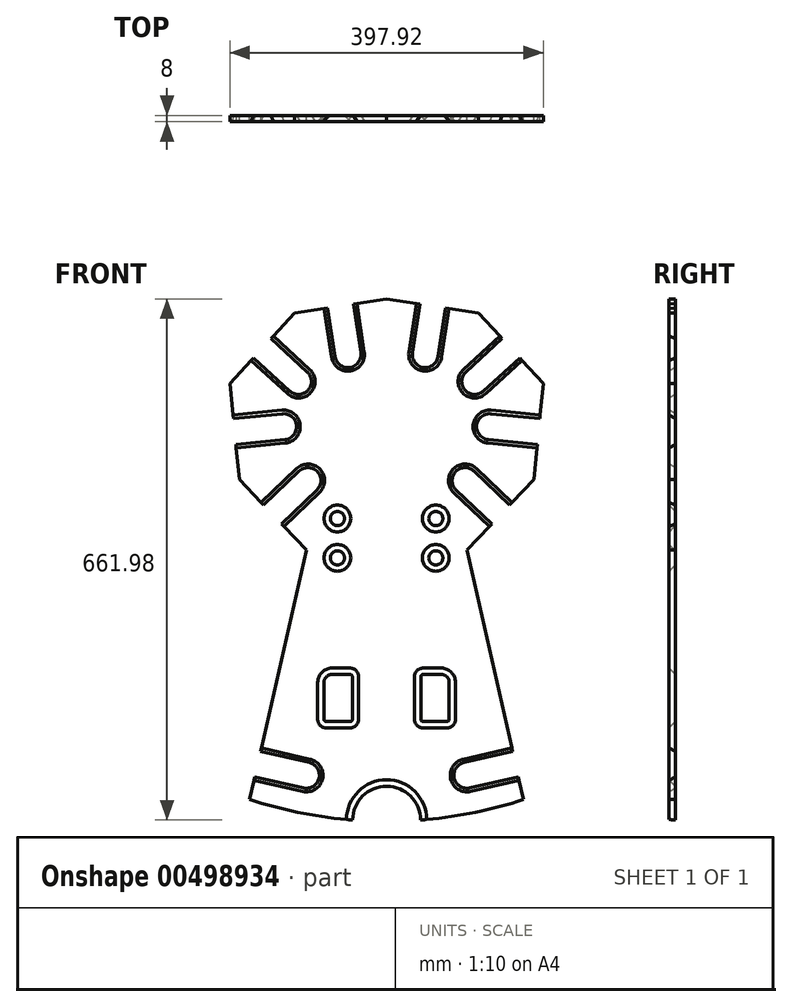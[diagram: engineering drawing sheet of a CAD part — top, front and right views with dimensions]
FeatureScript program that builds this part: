
annotation { "Feature Type Name" : "Feature", "Feature Type Description" : "" }
export const myFeature = defineFeature(function(context is Context, id is Id, definition is map)
    precondition{}
    {
        {
            var Q0;
            Q0=qCreatedBy(makeId("Front.planeOp"),FACE);
            var sketch = newSketch(context, id + "F0", { "sketchPlane" : qUnion([Q0])});
            skArc(sketch, "E0", {"start": v(43, -331) * mm, "mid": v(109.28, -321.9) * mm, "end": v(174, -305) * mm});
            skLineSegment(sketch, "E1", {"start": v(167.46, -276.23) * mm, "end": v(105.54, -290.3) * mm});
            skLineSegment(sketch, "E2", {"start": v(98.23, -258.12) * mm, "end": v(160.15, -244.05) * mm});
            skArc(sketch, "E3", {"start": v(98.23, -258.12) * mm, "mid": v(85.8, -277.87) * mm, "end": v(105.54, -290.3) * mm});
            skLineSegment(sketch, "E4", {"start": v(133.66, 45.23) * mm, "end": v(88.34, 88.26) * mm});
            skLineSegment(sketch, "E5", {"start": v(111.06, 112.2) * mm, "end": v(156.39, 69.16) * mm});
            skArc(sketch, "E6", {"start": v(111.06, 112.2) * mm, "mid": v(87.73, 111.59) * mm, "end": v(88.34, 88.26) * mm});
            skLineSegment(sketch, "E7", {"start": v(191.4, 146.18) * mm, "end": v(129.2, 152.25) * mm});
            skLineSegment(sketch, "E8", {"start": v(132.4, 185.1) * mm, "end": v(194.6, 179.02) * mm});
            skArc(sketch, "E9", {"start": v(132.4, 185.1) * mm, "mid": v(114.38, 170.27) * mm, "end": v(129.2, 152.25) * mm});
            skLineSegment(sketch, "E10", {"start": v(169.16, 256.17) * mm, "end": v(123.1, 213.93) * mm});
            skLineSegment(sketch, "E11", {"start": v(100.8, 238.26) * mm, "end": v(146.86, 280.5) * mm});
            skArc(sketch, "E12", {"start": v(100.8, 238.26) * mm, "mid": v(99.78, 214.95) * mm, "end": v(123.1, 213.93) * mm});
            skLineSegment(sketch, "E13", {"start": v(74.9, 319.52) * mm, "end": v(65.44, 257.74) * mm});
            skLineSegment(sketch, "E14", {"start": v(32.82, 262.74) * mm, "end": v(42.29, 324.52) * mm});
            skArc(sketch, "E15", {"start": v(32.82, 262.74) * mm, "mid": v(46.64, 243.93) * mm, "end": v(65.44, 257.74) * mm});
            skArc(sketch, "E16", {"start": v(-174, -305) * mm, "mid": v(-109.28, -321.9) * mm, "end": v(-43, -331) * mm});
            skLineSegment(sketch, "E17", {"start": v(-167.46, -276.23) * mm, "end": v(-105.54, -290.3) * mm});
            skLineSegment(sketch, "E18", {"start": v(-98.23, -258.12) * mm, "end": v(-160.15, -244.05) * mm});
            skArc(sketch, "E19", {"start": v(-105.54, -290.3) * mm, "mid": v(-85.8, -277.87) * mm, "end": v(-98.23, -258.12) * mm});
            skLineSegment(sketch, "E20", {"start": v(-133.66, 45.23) * mm, "end": v(-88.34, 88.26) * mm});
            skLineSegment(sketch, "E21", {"start": v(-111.06, 112.2) * mm, "end": v(-156.39, 69.16) * mm});
            skArc(sketch, "E22", {"start": v(-88.34, 88.26) * mm, "mid": v(-87.73, 111.59) * mm, "end": v(-111.06, 112.2) * mm});
            skLineSegment(sketch, "E23", {"start": v(-191.4, 146.18) * mm, "end": v(-129.2, 152.25) * mm});
            skLineSegment(sketch, "E24", {"start": v(-132.4, 185.1) * mm, "end": v(-194.6, 179.02) * mm});
            skArc(sketch, "E25", {"start": v(-129.2, 152.25) * mm, "mid": v(-114.38, 170.27) * mm, "end": v(-132.4, 185.1) * mm});
            skLineSegment(sketch, "E26", {"start": v(-169.16, 256.17) * mm, "end": v(-123.1, 213.93) * mm});
            skLineSegment(sketch, "E27", {"start": v(-100.8, 238.26) * mm, "end": v(-146.86, 280.5) * mm});
            skArc(sketch, "E28", {"start": v(-123.1, 213.93) * mm, "mid": v(-99.78, 214.95) * mm, "end": v(-100.8, 238.26) * mm});
            skLineSegment(sketch, "E29", {"start": v(-74.9, 319.52) * mm, "end": v(-65.44, 257.74) * mm});
            skLineSegment(sketch, "E30", {"start": v(-32.82, 262.74) * mm, "end": v(-42.29, 324.52) * mm});
            skArc(sketch, "E31", {"start": v(-65.44, 257.74) * mm, "mid": v(-46.64, 243.93) * mm, "end": v(-32.82, 262.74) * mm});
            skArc(sketch, "E32", {"start": v(43, -331) * mm, "mid": v(0, -288) * mm, "end": v(-43, -331) * mm});
            skCircle(sketch, "E33", {"center": v(-62.5, 52) * mm, "radius": 9 * mm});
            skCircle(sketch, "E34", {"center": v(62.5, 52) * mm, "radius": 9 * mm});
            skCircle(sketch, "E35", {"center": v(-62.5, 2) * mm, "radius": 9 * mm});
            skCircle(sketch, "E36", {"center": v(62.5, 2) * mm, "radius": 9 * mm});
            skLineSegment(sketch, "E37", {"start": v(-43.5, -146) * mm, "end": v(-43.5, -206) * mm});
            skLineSegment(sketch, "E38", {"start": v(43.5, -146) * mm, "end": v(43.5, -206) * mm});
            skLineSegment(sketch, "E39", {"start": v(-69.5, -146) * mm, "end": v(-43.5, -146) * mm});
            skLineSegment(sketch, "E40", {"start": v(-79.5, -206) * mm, "end": v(-43.5, -206) * mm});
            skLineSegment(sketch, "E41", {"start": v(-79.5, -156) * mm, "end": v(-79.5, -206) * mm});
            skLineSegment(sketch, "E42", {"start": v(79.5, -156) * mm, "end": v(79.5, -206) * mm});
            skLineSegment(sketch, "E43", {"start": v(43.5, -146) * mm, "end": v(69.5, -146) * mm});
            skLineSegment(sketch, "E44", {"start": v(43.5, -206) * mm, "end": v(79.5, -206) * mm});
            skArc(sketch, "E45", {"start": v(79.5, -156) * mm, "mid": v(76.57, -148.92) * mm, "end": v(69.5, -146) * mm});
            skArc(sketch, "E46", {"start": v(-69.5, -146) * mm, "mid": v(-76.57, -148.92) * mm, "end": v(-79.5, -156) * mm});
            skLineSegment(sketch, "E47", {"start": v(-133.66, 45.23) * mm, "end": v(-102, 11.87) * mm});
            skLineSegment(sketch, "E48", {"start": v(-187.04, 101.45) * mm, "end": v(-156.39, 69.16) * mm});
            skLineSegment(sketch, "E49", {"start": v(-191.4, 146.18) * mm, "end": v(-187.04, 101.45) * mm});
            skLineSegment(sketch, "E50", {"start": v(-198.96, 223.66) * mm, "end": v(-194.6, 179.02) * mm});
            skLineSegment(sketch, "E51", {"start": v(-169.16, 256.17) * mm, "end": v(-198.96, 223.66) * mm});
            skLineSegment(sketch, "E52", {"start": v(-117, 313.07) * mm, "end": v(-146.86, 280.5) * mm});
            skLineSegment(sketch, "E53", {"start": v(-74.9, 319.52) * mm, "end": v(-117, 313.07) * mm});
            skLineSegment(sketch, "E54", {"start": v(0, 331) * mm, "end": v(-42.29, 324.52) * mm});
            skLineSegment(sketch, "E55", {"start": v(0, 331) * mm, "end": v(42.29, 324.52) * mm});
            skLineSegment(sketch, "E56", {"start": v(74.9, 319.52) * mm, "end": v(117, 313.07) * mm});
            skLineSegment(sketch, "E57", {"start": v(117, 313.07) * mm, "end": v(146.86, 280.5) * mm});
            skLineSegment(sketch, "E58", {"start": v(169.16, 256.17) * mm, "end": v(198.96, 223.66) * mm});
            skLineSegment(sketch, "E59", {"start": v(198.96, 223.66) * mm, "end": v(194.6, 179.02) * mm});
            skLineSegment(sketch, "E60", {"start": v(191.4, 146.18) * mm, "end": v(187.04, 101.45) * mm});
            skLineSegment(sketch, "E61", {"start": v(187.04, 101.45) * mm, "end": v(156.39, 69.16) * mm});
            skLineSegment(sketch, "E62", {"start": v(133.66, 45.23) * mm, "end": v(102, 11.87) * mm});
            skLineSegment(sketch, "E63", {"start": v(-102, 11.87) * mm, "end": v(-160.15, -244.05) * mm});
            skLineSegment(sketch, "E64", {"start": v(102, 11.87) * mm, "end": v(160.15, -244.05) * mm});
            skLineSegment(sketch, "E65", {"start": v(-167.46, -276.23) * mm, "end": v(-174, -305) * mm});
            skLineSegment(sketch, "E66", {"start": v(167.46, -276.23) * mm, "end": v(174, -305) * mm});
            skSolve(sketch);
        }
        {
            var Q0;
            Q0 = qSketchRegion(id + "F0", true);
            extrude(context, id + "F1", {"entities" : qUnion([Q0]), "depth" : 8 * mm});
        }
        {
            var Q0;
            Q0=makeQuery(id+"F1.opExtrude","SWEPT_EDGE",EDGE,{"disambiguationData":[OSD([sQuery(id+"F0.wireOp",EDGE,"E37"),sQuery(id+"F0.wireOp",EDGE,"E40")])]});
            var Q1;
            Q1=makeQuery(id+"F1.opExtrude","SWEPT_EDGE",EDGE,{"disambiguationData":[OSD([sQuery(id+"F0.wireOp",EDGE,"E42"),sQuery(id+"F0.wireOp",EDGE,"E44")])]});
            var Q2;
            Q2=makeQuery(id+"F1.opExtrude","SWEPT_EDGE",EDGE,{"disambiguationData":[OSD([sQuery(id+"F0.wireOp",EDGE,"E38"),sQuery(id+"F0.wireOp",EDGE,"E44")])]});
            var Q3;
            Q3=makeQuery(id+"F1.opExtrude","SWEPT_EDGE",EDGE,{"disambiguationData":[OSD([sQuery(id+"F0.wireOp",EDGE,"E40"),sQuery(id+"F0.wireOp",EDGE,"E41")])]});
            var Q4;
            Q4=makeQuery(id+"F1.opExtrude","SWEPT_EDGE",EDGE,{"disambiguationData":[OSD([sQuery(id+"F0.wireOp",EDGE,"E37"),sQuery(id+"F0.wireOp",EDGE,"E39")])]});
            var Q5;
            Q5=makeQuery(id+"F1.opExtrude","SWEPT_EDGE",EDGE,{"disambiguationData":[OSD([sQuery(id+"F0.wireOp",EDGE,"E38"),sQuery(id+"F0.wireOp",EDGE,"E43")])]});
            fillet(context, id + "F2", {"entities" : qUnion([Q0, Q1, Q2, Q3, Q4, Q5]), "radius" : 3 * mm, "tangentPropagation" : true, "allowEdgeOverflow" : false});
        }
        {
            var Q0;
            Q0=makeQuery(id+"F1.opExtrude","CAP_EDGE",EDGE,{"disambiguationData":[OSD([sQuery(id+"F0.wireOp",EDGE,"E33")])],"isStart":false});
            var Q1;
            Q1=makeQuery(id+"F1.opExtrude","CAP_EDGE",EDGE,{"disambiguationData":[OSD([sQuery(id+"F0.wireOp",EDGE,"E34")])],"isStart":false});
            var Q2;
            Q2=makeQuery(id+"F1.opExtrude","CAP_EDGE",EDGE,{"disambiguationData":[OSD([sQuery(id+"F0.wireOp",EDGE,"E35")])],"isStart":false});
            var Q3;
            Q3=makeQuery(id+"F1.opExtrude","CAP_EDGE",EDGE,{"disambiguationData":[OSD([sQuery(id+"F0.wireOp",EDGE,"E36")])],"isStart":false});
            var Q4;
            Q4=makeQuery(id+"F1.opExtrude","CAP_EDGE",EDGE,{"disambiguationData":[OSD([sQuery(id+"F0.wireOp",EDGE,"E39")])],"isStart":false});
            var Q5;
            Q5=makeQuery(id+"F1.opExtrude","CAP_EDGE",EDGE,{"disambiguationData":[OSD([sQuery(id+"F0.wireOp",EDGE,"E43")])],"isStart":false});
            var Q6;
            Q6=makeQuery(id+"F1.opExtrude","CAP_EDGE",EDGE,{"disambiguationData":[OSD([sQuery(id+"F0.wireOp",EDGE,"E32")])],"isStart":false});
            chamfer(context, id + "F3", {"entities" : qUnion([Q0, Q1, Q2, Q3, Q4, Q5, Q6]), "width" : 8 * mm, "tangentPropagation" : true});
        }
        {
            var Q0;
            Q0=makeQuery(id+"F1.opExtrude","CAP_EDGE",EDGE,{"disambiguationData":[OSD([sQuery(id+"F0.wireOp",EDGE,"E21")])],"isStart":false});
            var Q1;
            Q1=makeQuery(id+"F1.opExtrude","CAP_EDGE",EDGE,{"disambiguationData":[OSD([sQuery(id+"F0.wireOp",EDGE,"E24")])],"isStart":false});
            var Q2;
            Q2=makeQuery(id+"F1.opExtrude","CAP_EDGE",EDGE,{"disambiguationData":[OSD([sQuery(id+"F0.wireOp",EDGE,"E27")])],"isStart":false});
            var Q3;
            Q3=makeQuery(id+"F1.opExtrude","CAP_EDGE",EDGE,{"disambiguationData":[OSD([sQuery(id+"F0.wireOp",EDGE,"E30")])],"isStart":false});
            var Q4;
            Q4=makeQuery(id+"F1.opExtrude","CAP_EDGE",EDGE,{"disambiguationData":[OSD([sQuery(id+"F0.wireOp",EDGE,"E13")])],"isStart":false});
            var Q5;
            Q5=makeQuery(id+"F1.opExtrude","CAP_EDGE",EDGE,{"disambiguationData":[OSD([sQuery(id+"F0.wireOp",EDGE,"E11")])],"isStart":false});
            var Q6;
            Q6=makeQuery(id+"F1.opExtrude","CAP_EDGE",EDGE,{"disambiguationData":[OSD([sQuery(id+"F0.wireOp",EDGE,"E8")])],"isStart":false});
            var Q7;
            Q7=makeQuery(id+"F1.opExtrude","CAP_EDGE",EDGE,{"disambiguationData":[OSD([sQuery(id+"F0.wireOp",EDGE,"E5")])],"isStart":false});
            var Q8;
            Q8=makeQuery(id+"F1.opExtrude","CAP_EDGE",EDGE,{"disambiguationData":[OSD([sQuery(id+"F0.wireOp",EDGE,"E2")])],"isStart":false});
            var Q9;
            Q9=makeQuery(id+"F1.opExtrude","CAP_EDGE",EDGE,{"disambiguationData":[OSD([sQuery(id+"F0.wireOp",EDGE,"E18")])],"isStart":false});
            chamfer(context, id + "F4", {"entities" : qUnion([Q0, Q1, Q2, Q3, Q4, Q5, Q6, Q7, Q8, Q9]), "chamferType" : ChamferType.OFFSET_ANGLE, "width" : 4.5 * mm, "oppositeDirection" : true, "angle" : 60 * degree, "tangentPropagation" : true});
        }
    });
